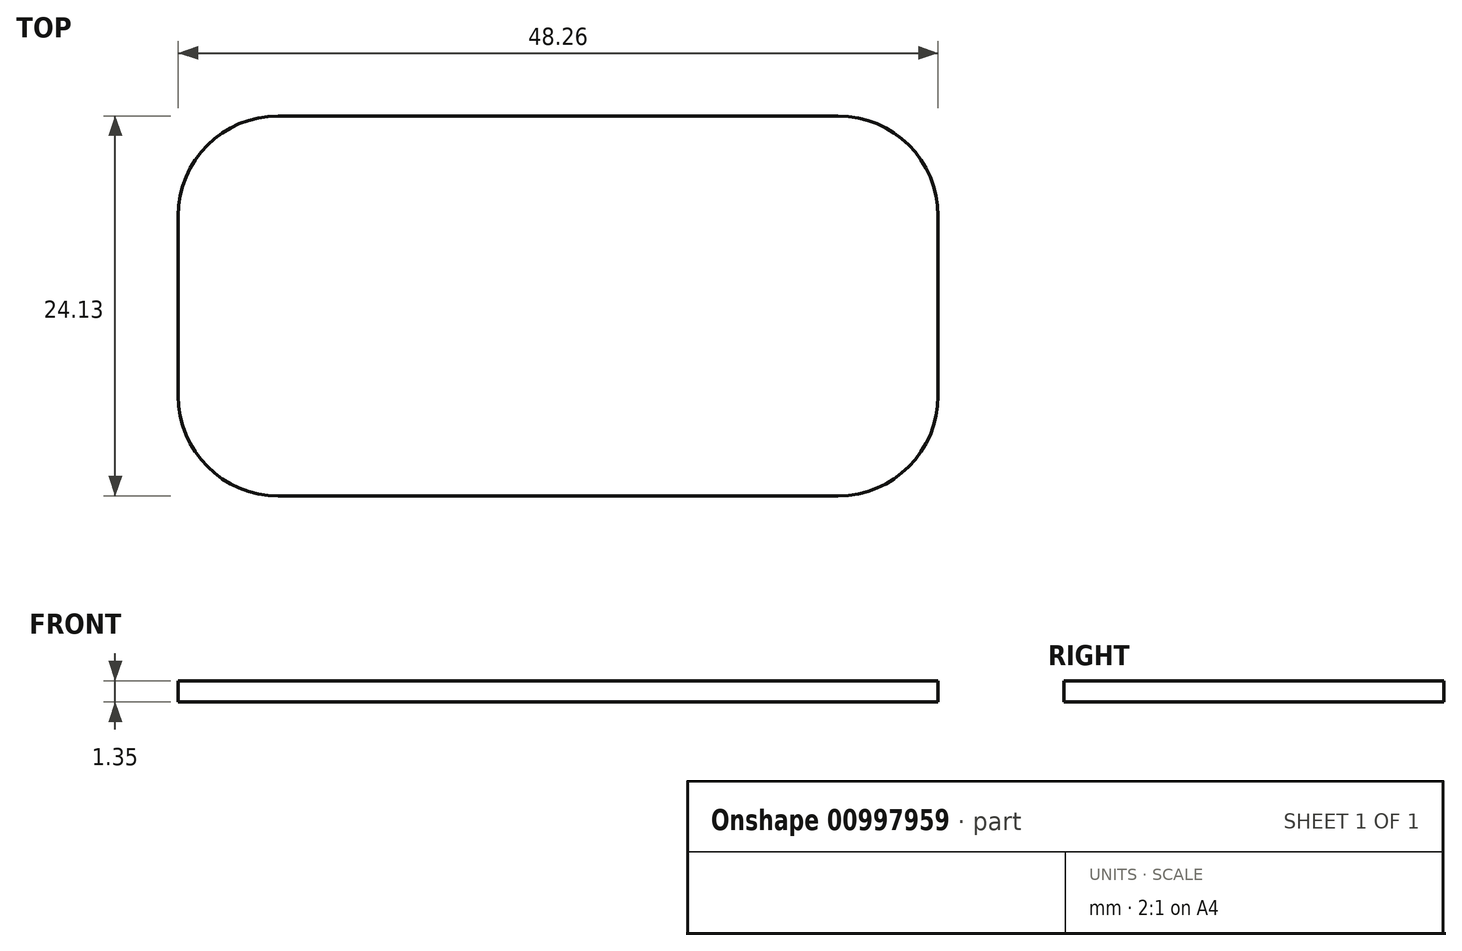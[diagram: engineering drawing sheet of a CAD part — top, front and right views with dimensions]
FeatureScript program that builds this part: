
annotation { "Feature Type Name" : "Feature", "Feature Type Description" : "" }
export const myFeature = defineFeature(function(context is Context, id is Id, definition is map)
    precondition{}
    {
        {
            var Q0;
            Q0=qCreatedBy(makeId("Top.planeOp"),FACE);
            var sketch = newSketch(context, id + "F0", { "sketchPlane" : qUnion([Q0])});
            skLineSegment(sketch, "E0.bottom", {"start": v(-13.24, -6.7) * mm, "end": v(22.32, -6.7) * mm});
            skLineSegment(sketch, "E0.top", {"start": v(-13.24, 17.44) * mm, "end": v(22.32, 17.44) * mm});
            skLineSegment(sketch, "E0.left", {"start": v(-19.6, -0.34) * mm, "end": v(-19.6, 11.09) * mm});
            skLineSegment(sketch, "E0.right", {"start": v(28.67, -0.34) * mm, "end": v(28.67, 11.09) * mm});
            skPoint(sketch, "E1.visualSharp", {"position": v(28.67, 17.44) * mm});
            skArc(sketch, "E1.filletArc", {"start": v(28.67, 11.09) * mm, "mid": v(26.8, 15.58) * mm, "end": v(22.32, 17.44) * mm});
            skPoint(sketch, "E2.visualSharp", {"position": v(28.67, -6.7) * mm});
            skArc(sketch, "E2.filletArc", {"start": v(22.32, -6.7) * mm, "mid": v(26.8, -4.83) * mm, "end": v(28.67, -0.34) * mm});
            skPoint(sketch, "E3.visualSharp", {"position": v(-19.6, -6.7) * mm});
            skArc(sketch, "E3.filletArc", {"start": v(-19.6, -0.34) * mm, "mid": v(-17.73, -4.83) * mm, "end": v(-13.24, -6.7) * mm});
            skPoint(sketch, "E4.visualSharp", {"position": v(-19.6, 17.44) * mm});
            skArc(sketch, "E4.filletArc", {"start": v(-13.24, 17.44) * mm, "mid": v(-17.73, 15.58) * mm, "end": v(-19.6, 11.09) * mm});
            skSolve(sketch);
        }
        {
            var Q0;
            Q0=makeQuery(id+"F0.imprint","IMPRINT",FACE,{"disambiguationData":[TD([[makeQuery(id+"F0.imprint","IMPRINT",EDGE,{"derivedFrom":sQuery(id+"F0.wireOp",EDGE,"E0.bottom")}),1.0]])]});
            extrude(context, id + "F1", {"entities" : qUnion([Q0]), "depth" : 1.35 * mm, "offsetDistance" : 25 * mm});
        }
    });
